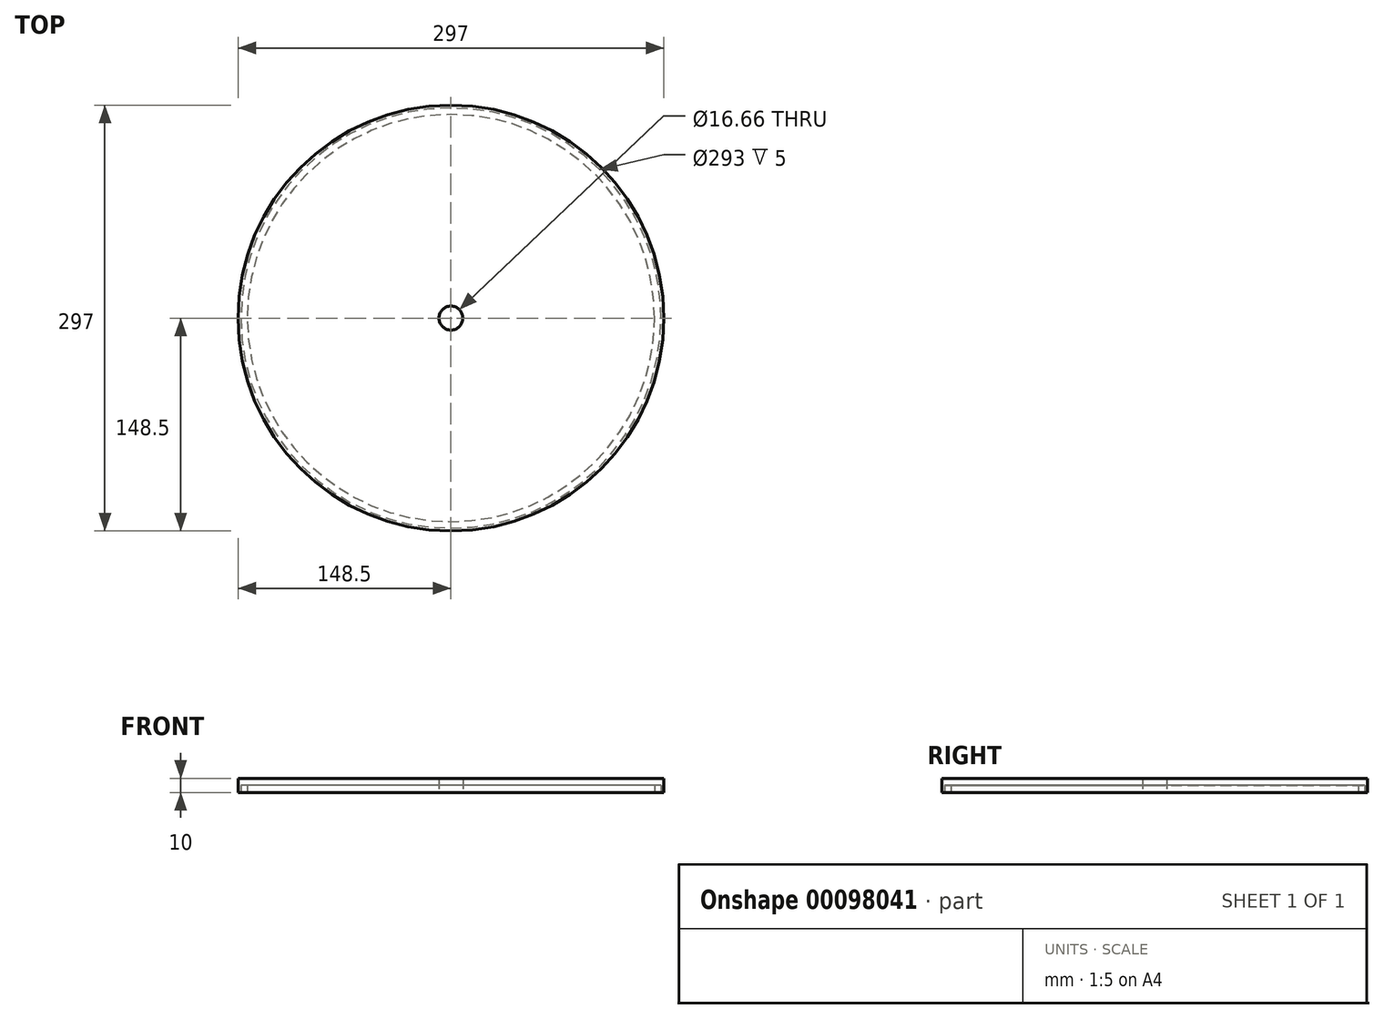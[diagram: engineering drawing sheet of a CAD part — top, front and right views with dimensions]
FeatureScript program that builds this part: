
annotation { "Feature Type Name" : "Feature", "Feature Type Description" : "" }
export const myFeature = defineFeature(function(context is Context, id is Id, definition is map)
    precondition{}
    {
        {
            var Q0;
            Q0=qCreatedBy(makeId("Top.planeOp"),FACE);
            var sketch = newSketch(context, id + "F0", { "sketchPlane" : qUnion([Q0])});
            skCircle(sketch, "E0", {"center": v(0, 0) * mm, "radius": 148.5 * mm});
            skCircle(sketch, "E1", {"center": v(0, 0) * mm, "radius": 8.33 * mm});
            skSolve(sketch);
        }
        {
            var Q0;
            Q0=makeQuery(id+"F0.imprint","IMPRINT",FACE,{"disambiguationData":[TD([[makeQuery(id+"F0.imprint","IMPRINT",EDGE,{"derivedFrom":sQuery(id+"F0.wireOp",EDGE,"E0")}),1.0]])]});
            var Q1;
            Q1=makeQuery(id+"F0.imprint","IMPRINT",FACE,{"disambiguationData":[TD([[makeQuery(id+"F0.imprint","IMPRINT",EDGE,{"derivedFrom":sQuery(id+"F0.wireOp",EDGE,"LIXrByum-44Gz-KbWN-PE50-DMeDG7NppI0J")}),1.0]])]});
            var Q2;
            Q2=makeQuery(id+"F0.imprint","IMPRINT",FACE,{"disambiguationData":[TD([[makeQuery(id+"F0.imprint","IMPRINT",EDGE,{"derivedFrom":sQuery(id+"F0.wireOp",EDGE,"oq2Y4278-V4UZ-WgQw-2GIa-DsGsglEtdsp5")}),1.0]])]});
            extrude(context, id + "F1", {"entities" : qUnion([Q0, Q1, Q2]), "depth" : 10 * mm});
        }
        {
            var Q0;
            Q0=makeQuery(id+"F0.imprint","IMPRINT",FACE,{"disambiguationData":[TD([[makeQuery(id+"F0.imprint","IMPRINT",EDGE,{"derivedFrom":sQuery(id+"F0.wireOp",EDGE,"E0")}),1.0]])]});
            var sketch = newSketch(context, id + "F2", { "sketchPlane" : qUnion([Q0])});
            skCircle(sketch, "E2", {"center": v(0, 0) * mm, "radius": 146.5 * mm});
            skCircle(sketch, "E3", {"center": v(0, 0) * mm, "radius": 142 * mm});
            skSolve(sketch);
        }
        {
            var Q0;
            Q0=qSketchRegion(id+"F2",true);
            extrude(context, id + "F3", {"entities" : qUnion([Q0]), "operationType" : NewBodyOperationType.REMOVE, "depth" : 5 * mm});
        }
    });
